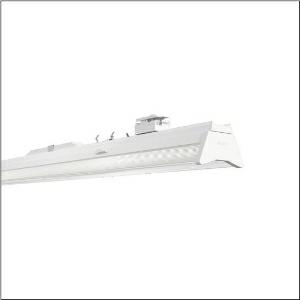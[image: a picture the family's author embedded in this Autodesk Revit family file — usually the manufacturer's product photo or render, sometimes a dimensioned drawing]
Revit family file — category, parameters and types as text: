
# Revit family: licross_21_performance_ho_52tm16mn4e5m
name_source: partatom
category: Lighting Fixtures
units: mm (PartAtom-declared; Revit-internal decimal feet)

## family parameters
Cut with Voids When Loaded = No
Host = Face
Light Source = No
Part Type = Normal
Room Calculation Point = No
Round Connector Dimension = Use Diameter
Shared = No

## types (1)
- --- (1 x LED, 14970 lm, 83.2 W, 4000K)
    Apparent Load = 83 VA
    CIE Flux Codes = 63 87 95 78 100
    Color Rendering = 80
    Color Temperature = 4000K
    Default Elevation = 1800 mm
    Description = Licross 21 Performance HO, luminaire insert, of sheet steel, galvanised, coil coated, white, length: 1.500mm, width: 120mm, height: 123mm, LED rated luminous flux: 14.970lm, light colour: 840, SDCM (Standard Deviation of Colour Matching)MacAdam ≤ 3 SDCM (initial), control gear: ON/OFF Multilumen, with plug, 3-pole, with phase selection, mains connection: 220..240V, AC, 50/60Hz, rated input power: 83W, internal wiring halogen-free, primary light control with lens, of plastic, primary optical cover: cover, of PMMA, light emission: direct/indirect distribution, primary light characteristic: symmetric, protection rating (complete): IP40, insulation class (complete): insulation class I (protective earthing), certification: CE, ENEC, UKCA, protection symbol: D if used in an environment without relevant dust loads with corresponding accessories, impact resistance: IK06, permissible ambient temperature for indoor applications: -35..+35°C, corresponds to IFS (International Featured Standards) requirements for safety and quality in the food industry, reducing of maximum allowable ambient temperature of 5°C with ceiling mounting, LABS conformity tested according to VDMA 24364:2018-05, The light source and the operating device comply with the requirements of the Ecodesign Regulation (EU) 2019/2020 and are replaceable in accordance with this regulation, packaging unit: 1 piece
    Height = 114 mm
    Lamp = 1 x LED
    Lamp Light Flux = 14970 lm
    Lamp Power = 83.2 W
    Lamp count = 1
    Length = 1500 mm
    Luminous efficacy = 180 lm/W
    Manufacturer = Siteco
    ModVariant = No
    Model = 52TM16MN4E5M
    Mounting Place = Ceiling
    Mounting Type = Pendant
    Number of Poles = 1
    OnlyDefault = Yes
    Power Factor = 1
    Product Name = Licross 21 Performance HO
    Product group = luminaire insert | ceiling pendant
    ProductGroupID = 901
    Protection Class = Protection class I
    Protection Degree = IP 40
    RLX_Detail_Level = 1
    RLX_Emergency_Light_Flux = 0 lm
    RLX_Emergency_Type = 0
    RLX_Emergency_Type_DB = No
    RlxData = <blob elided: 32069 chars, md5=4b6b76f7>
    Socket = socket
    Standby Power = 0 W
    System Light Flux = 14970 lm
    System Power = 83 W
    Type Comments = factory setting: luminous flux: 100 % | (A | C | E) | 195 mA
    Type Image = l_1256138.jpg
    URL = http://relux.com
    VarID = @adj_109201
    Voltage = 0 V
    Weight = 0.00 kg
    Width = 120 mm

## geometry (parser evidence)
native form markers: Blend x4, Sweep x13
no freeform markers — native parametric forms only
